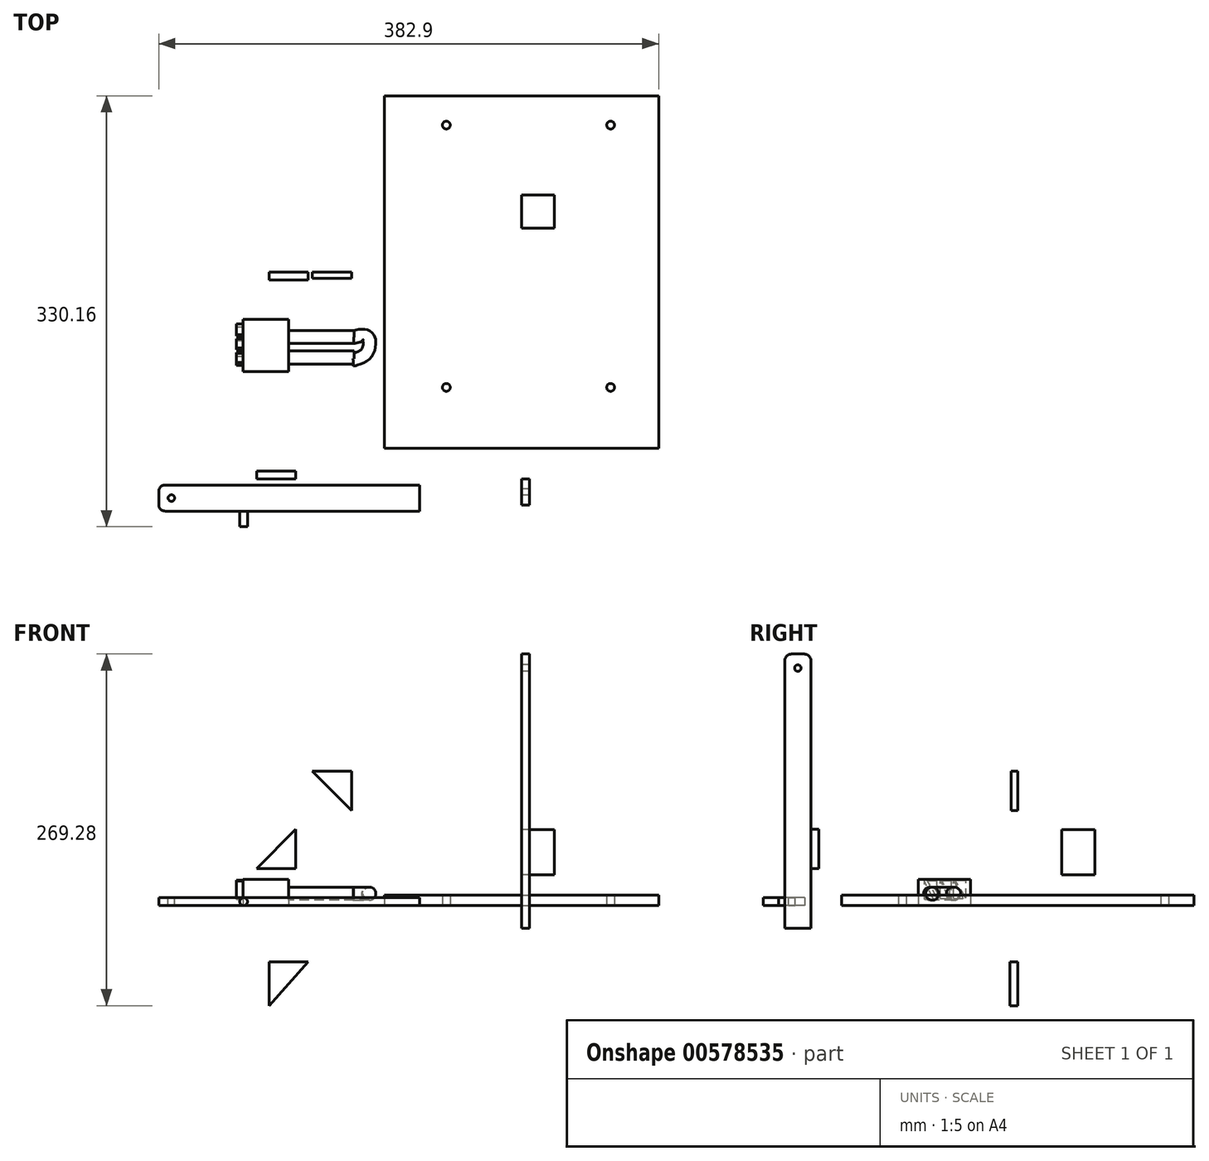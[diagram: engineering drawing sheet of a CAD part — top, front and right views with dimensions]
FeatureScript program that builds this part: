
annotation { "Feature Type Name" : "Feature", "Feature Type Description" : "" }
export const myFeature = defineFeature(function(context is Context, id is Id, definition is map)
    precondition{}
    {
        {
            var Q0;
            Q0=qCreatedBy(makeId("Top.planeOp"),FACE);
            var sketch = newSketch(context, id + "F0", { "sketchPlane" : qUnion([Q0])});
            skLineSegment(sketch, "E0.bottom", {"start": v(135, -105) * mm, "end": v(-135, -105) * mm});
            skLineSegment(sketch, "E0.top", {"start": v(135, 105) * mm, "end": v(-135, 105) * mm});
            skLineSegment(sketch, "E0.left", {"start": v(135, -105) * mm, "end": v(135, 105) * mm});
            skLineSegment(sketch, "E0.right", {"start": v(-135, -105) * mm, "end": v(-135, 105) * mm});
            skPoint(sketch, "E0.middle", {"position": v(0, 0) * mm});
            skCircle(sketch, "E1", {"center": v(-117.17, 88.39) * mm, "radius": 3 * mm});
            skCircle(sketch, "E2", {"center": v(-96.1, 99.53) * mm, "radius": 3 * mm});
            skCircle(sketch, "E3", {"center": v(-57.59, 112.52) * mm, "radius": 3 * mm});
            skCircle(sketch, "E4", {"center": v(68.25, 112.52) * mm, "radius": 3 * mm});
            skPoint(sketch, "E5", {"position": v(0, 112.52) * mm});
            skPoint(sketch, "E6", {"position": v(-57.59, -88.4) * mm});
            skCircle(sketch, "E7", {"center": v(-57.59, -88.4) * mm, "radius": 3 * mm});
            skPoint(sketch, "E8", {"position": v(68.25, -88.4) * mm});
            skCircle(sketch, "E9", {"center": v(68.25, -88.4) * mm, "radius": 3 * mm});
            skSolve(sketch);
        }
        {
            var Q0;
            Q0=makeQuery(id+"F0.imprint","IMPRINT",FACE,{"disambiguationData":[TD([[makeQuery(id+"F0.imprint","IMPRINT",EDGE,{"derivedFrom":sQuery(id+"F0.wireOp",EDGE,"E0.bottom")}),-1.0]])]});
            var sketch = newSketch(context, id + "F1", { "sketchPlane" : qUnion([Q0])});
            skCircle(sketch, "E10", {"center": v(176.37, 242.82) * mm, "radius": 60 * mm});
            skSolve(sketch);
        }
        {
            var Q0;
            Q0=makeQuery(id+"F0.imprint","IMPRINT",FACE,{"disambiguationData":[TD([[makeQuery(id+"F0.imprint","IMPRINT",EDGE,{"derivedFrom":sQuery(id+"F0.wireOp",EDGE,"E0.bottom")}),-1.0]])]});
            var sketch = newSketch(context, id + "F2", { "sketchPlane" : qUnion([Q0])});
            skLineSegment(sketch, "E11.bottom", {"start": v(-77.9, -163.16) * mm, "end": v(-277.9, -163.16) * mm});
            skLineSegment(sketch, "E11.top", {"start": v(-77.9, -183.16) * mm, "end": v(-277.9, -183.16) * mm});
            skLineSegment(sketch, "E11.left", {"start": v(-77.9, -163.16) * mm, "end": v(-77.9, -183.16) * mm});
            skLineSegment(sketch, "E11.right", {"start": v(-277.9, -163.16) * mm, "end": v(-277.9, -183.16) * mm});
            skPoint(sketch, "E11.middle", {"position": v(-177.9, -173.16) * mm});
            skSolve(sketch);
        }
        {
            var Q0;
            Q0=qCreatedBy(makeId("Right.planeOp"),FACE);
            var sketch = newSketch(context, id + "F3", { "sketchPlane" : qUnion([Q0])});
            skLineSegment(sketch, "E12.bottom", {"start": v(-158.53, -17.4) * mm, "end": v(-178.53, -17.4) * mm});
            skLineSegment(sketch, "E12.top", {"start": v(-158.53, 192.6) * mm, "end": v(-178.53, 192.6) * mm});
            skLineSegment(sketch, "E12.left", {"start": v(-158.53, -17.4) * mm, "end": v(-158.53, 192.6) * mm});
            skLineSegment(sketch, "E12.right", {"start": v(-178.53, -17.4) * mm, "end": v(-178.53, 192.6) * mm});
            skPoint(sketch, "E12.middle", {"position": v(-168.53, 87.6) * mm});
            skSolve(sketch);
        }
        {
            var Q0;
            Q0=makeQuery(id+"F2.imprint","IMPRINT",FACE,{"disambiguationData":[TD([[makeQuery(id+"F2.imprint","IMPRINT",EDGE,{"derivedFrom":sQuery(id+"F2.wireOp",EDGE,"E11.bottom")}),1.0]])]});
            extrude(context, id + "F4", {"entities" : qUnion([Q0]), "depth" : 6 * mm, "offsetDistance" : 25 * mm});
        }
        {
            var Q0;
            Q0=makeQuery(id+"F3.imprint","IMPRINT",FACE,{"disambiguationData":[TD([[makeQuery(id+"F3.imprint","IMPRINT",EDGE,{"derivedFrom":sQuery(id+"F3.wireOp",EDGE,"E12.bottom")}),-1.0]])]});
            extrude(context, id + "F5", {"entities" : qUnion([Q0]), "depth" : 6 * mm, "offsetDistance" : 25 * mm});
        }
        {
            var Q0;
            Q0=makeQuery(id+"F4.opExtrude","CAP_FACE",FACE,{"disambiguationData":[OSD([sQuery(id+"F2.wireOp",EDGE,"E11.bottom"),sQuery(id+"F2.wireOp",EDGE,"E11.top"),sQuery(id+"F2.wireOp",EDGE,"E11.left"),sQuery(id+"F2.wireOp",EDGE,"E11.right")])],"isStart":false});
            var sketch = newSketch(context, id + "F6", { "sketchPlane" : qUnion([Q0])});
            skLineSegment(sketch, "E13.0.0", {"start": v(-277.9, -183.16) * mm, "end": v(-77.9, -183.16) * mm});
            skLineSegment(sketch, "E13.0.1", {"start": v(-77.9, -183.16) * mm, "end": v(-77.9, -163.16) * mm});
            skLineSegment(sketch, "E13.0.2", {"start": v(-77.9, -163.16) * mm, "end": v(-277.9, -163.16) * mm});
            skLineSegment(sketch, "E13.0.3", {"start": v(-277.9, -163.16) * mm, "end": v(-277.9, -183.16) * mm});
            skPoint(sketch, "E14", {"position": v(-268.17, -173.16) * mm});
            skPoint(sketch, "E14.positionSnap0", {"position": v(-277.9, -173.16) * mm});
            skSolve(sketch);
        }
        {
            var Q0;
            Q0=sQuery(id+"F6.wireOp",VERTEX,"E14");
            var Q1;
            Q1=makeQuery(id+"F4.opExtrude","SWEPT_BODY",BODY,{"disambiguationData":[OSD([sQuery(id+"F2.wireOp",EDGE,"E11.bottom"),sQuery(id+"F2.wireOp",EDGE,"E11.top"),sQuery(id+"F2.wireOp",EDGE,"E11.left"),sQuery(id+"F2.wireOp",EDGE,"E11.right")])]});
            hole(context, id + "F7", {"style" : HoleStyle.SIMPLE, "endStyle" : HoleEndStyle.THROUGH, "holeDiameter" : 5 * mm, "isTappedThrough" : true, "tappedDepth" : 12 * mm, "tapClearance" : 3, "locations" : qUnion([Q0]), "scope" : qUnion([Q1])});
        }
        {
            var Q0;
            Q0=makeQuery(id+"F5.opExtrude","CAP_FACE",FACE,{"disambiguationData":[OSD([sQuery(id+"F3.wireOp",EDGE,"E12.bottom"),sQuery(id+"F3.wireOp",EDGE,"E12.top"),sQuery(id+"F3.wireOp",EDGE,"E12.left"),sQuery(id+"F3.wireOp",EDGE,"E12.right")])],"isStart":true});
            var sketch = newSketch(context, id + "F8", { "sketchPlane" : qUnion([Q0])});
            skLineSegment(sketch, "E15.0.0", {"start": v(158.53, 192.6) * mm, "end": v(158.53, -17.4) * mm});
            skLineSegment(sketch, "E15.0.1", {"start": v(158.53, -17.4) * mm, "end": v(178.53, -17.4) * mm});
            skLineSegment(sketch, "E15.0.2", {"start": v(178.53, -17.4) * mm, "end": v(178.53, 192.6) * mm});
            skLineSegment(sketch, "E15.0.3", {"start": v(178.53, 192.6) * mm, "end": v(158.53, 192.6) * mm});
            skPoint(sketch, "E16", {"position": v(168.53, 181.87) * mm});
            skPoint(sketch, "E16.positionSnap0", {"position": v(168.53, 192.6) * mm});
            skSolve(sketch);
        }
        {
            var Q0;
            Q0=sQuery(id+"F8.wireOp",VERTEX,"E16");
            var Q1;
            Q1=makeQuery(id+"F5.opExtrude","SWEPT_BODY",BODY,{"disambiguationData":[OSD([sQuery(id+"F3.wireOp",EDGE,"E12.bottom"),sQuery(id+"F3.wireOp",EDGE,"E12.top"),sQuery(id+"F3.wireOp",EDGE,"E12.left"),sQuery(id+"F3.wireOp",EDGE,"E12.right")])]});
            hole(context, id + "F9", {"style" : HoleStyle.SIMPLE, "endStyle" : HoleEndStyle.THROUGH, "holeDiameter" : 5 * mm, "isTappedThrough" : true, "tappedDepth" : 12 * mm, "tapClearance" : 3, "locations" : qUnion([Q0]), "scope" : qUnion([Q1])});
        }
        {
            var Q0;
            Q0=makeQuery(id+"F5.opExtrude","SWEPT_EDGE",EDGE,{"disambiguationData":[OSD([sQuery(id+"F3.wireOp",EDGE,"E12.top"),sQuery(id+"F3.wireOp",EDGE,"E12.right")])]});
            fillet(context, id + "F10", {"entities" : qUnion([Q0]), "radius" : 5 * mm, "tangentPropagation" : true, "allowEdgeOverflow" : false});
        }
        {
            var Q0;
            Q0=makeQuery(id+"F5.opExtrude","SWEPT_EDGE",EDGE,{"disambiguationData":[OSD([sQuery(id+"F3.wireOp",EDGE,"E12.top"),sQuery(id+"F3.wireOp",EDGE,"E12.left")])]});
            fillet(context, id + "F11", {"entities" : qUnion([Q0]), "radius" : 5 * mm, "tangentPropagation" : true, "allowEdgeOverflow" : false});
        }
        {
            var Q0;
            Q0=makeQuery(id+"F4.opExtrude","SWEPT_EDGE",EDGE,{"disambiguationData":[OSD([sQuery(id+"F2.wireOp",EDGE,"E11.top"),sQuery(id+"F2.wireOp",EDGE,"E11.right")])]});
            fillet(context, id + "F12", {"entities" : qUnion([Q0]), "radius" : 5 * mm, "tangentPropagation" : true, "allowEdgeOverflow" : false});
        }
        {
            var Q0;
            Q0=makeQuery(id+"F4.opExtrude","SWEPT_EDGE",EDGE,{"disambiguationData":[OSD([sQuery(id+"F2.wireOp",EDGE,"E11.bottom"),sQuery(id+"F2.wireOp",EDGE,"E11.right")])]});
            fillet(context, id + "F13", {"entities" : qUnion([Q0]), "radius" : 5 * mm, "tangentPropagation" : true, "allowEdgeOverflow" : false});
        }
        {
            var Q0;
            Q0=makeQuery(id+"F0.imprint","IMPRINT",FACE,{"disambiguationData":[TD([[makeQuery(id+"F0.imprint","IMPRINT",EDGE,{"derivedFrom":sQuery(id+"F0.wireOp",EDGE,"E0.bottom")}),-1.0]])]});
            var sketch = newSketch(context, id + "F14", { "sketchPlane" : qUnion([Q0])});
            skLineSegment(sketch, "E17.bottom", {"start": v(-105, -135) * mm, "end": v(105, -135) * mm});
            skLineSegment(sketch, "E17.top", {"start": v(-105, 135) * mm, "end": v(105, 135) * mm});
            skLineSegment(sketch, "E17.left", {"start": v(-105, -135) * mm, "end": v(-105, 135) * mm});
            skLineSegment(sketch, "E17.right", {"start": v(105, -135) * mm, "end": v(105, 135) * mm});
            skPoint(sketch, "E17.middle", {"position": v(0, 0) * mm});
            skSolve(sketch);
        }
        {
            var Q0;
            Q0 = qSketchRegion(id + "F14", true);
            extrude(context, id + "F15", {"entities" : qUnion([Q0]), "depth" : 8 * mm, "offsetDistance" : 25 * mm});
        }
        {
            var Q0;
            Q0=makeQuery(id+"F4.opExtrude","SWEPT_FACE",FACE,{"disambiguationData":[OSD([sQuery(id+"F2.wireOp",EDGE,"E11.top")])]});
            var sketch = newSketch(context, id + "F16", { "sketchPlane" : qUnion([Q0])});
            skLineSegment(sketch, "E18", {"start": v(-272.9, 0) * mm, "end": v(-212.9, 0) * mm});
            skLineSegment(sketch, "E19", {"start": v(-212.9, 0) * mm, "end": v(-212.9, 6) * mm});
            skCircle(sketch, "E20", {"center": v(-212.9, 3) * mm, "radius": 3 * mm});
            skSolve(sketch);
        }
        {
            var Q0;
            {var subQ0=sQuery(id+"F16.wireOp",EDGE,"E19");Q0=makeQuery(id+"F16.imprint","IMPRINT",FACE,{"disambiguationData":[TD([[makeQuery(id+"F16.imprint","IMPRINT",EDGE,{"derivedFrom":subQ0}),-1.0]])]});}
            var Q1;
            {var subQ0=sQuery(id+"F16.wireOp",EDGE,"E19");Q1=makeQuery(id+"F16.imprint","IMPRINT",FACE,{"disambiguationData":[TD([[makeQuery(id+"F16.imprint","IMPRINT",EDGE,{"derivedFrom":subQ0}),1.0]])]});}
            extrude(context, id + "F17", {"entities" : qUnion([Q0, Q1]), "operationType" : NewBodyOperationType.ADD, "depth" : 12 * mm, "offsetDistance" : 25 * mm});
        }
        {
            var Q0;
            Q0=makeQuery(id+"F1.imprint","IMPRINT",FACE,{"disambiguationData":[TD([[makeQuery(id+"F1.imprint","IMPRINT",EDGE,{"derivedFrom":sQuery(id+"F1.wireOp",EDGE,"E10")}),1.0]])]});
            extrude(context, id + "F18", {"entities" : qUnion([Q0]), "depth" : 6 * mm, "offsetDistance" : 25 * mm});
        }
        {
            var Q0;
            Q0=qCreatedBy(makeId("Right.planeOp"),FACE);
            var sketch = newSketch(context, id + "F19", { "sketchPlane" : qUnion([Q0])});
            skLineSegment(sketch, "E21.bottom", {"start": v(59.06, 58.09) * mm, "end": v(33.68, 58.09) * mm});
            skLineSegment(sketch, "E21.top", {"start": v(59.06, 23.62) * mm, "end": v(33.68, 23.62) * mm});
            skLineSegment(sketch, "E21.left", {"start": v(59.06, 58.09) * mm, "end": v(59.06, 23.62) * mm});
            skLineSegment(sketch, "E21.right", {"start": v(33.68, 58.09) * mm, "end": v(33.68, 23.62) * mm});
            skSolve(sketch);
        }
        {
            var Q0;
            Q0 = qSketchRegion(id + "F19", true);
            extrude(context, id + "F20", {"entities" : qUnion([Q0]), "depth" : 25 * mm, "offsetDistance" : 25 * mm});
        }
        {
            var Q0;
            Q0=makeQuery(id+"F5.opExtrude","SWEPT_FACE",FACE,{"disambiguationData":[OSD([sQuery(id+"F3.wireOp",EDGE,"E12.left")])]});
            var sketch = newSketch(context, id + "F21", { "sketchPlane" : qUnion([Q0])});
            skLineSegment(sketch, "E22", {"start": v(202.9, 28.37) * mm, "end": v(172.9, 28.37) * mm});
            skLineSegment(sketch, "E23", {"start": v(172.9, 28.37) * mm, "end": v(172.9, 58.37) * mm});
            skLineSegment(sketch, "E24", {"start": v(172.9, 58.37) * mm, "end": v(202.9, 28.37) * mm});
            skSolve(sketch);
        }
        {
            var Q0;
            Q0=makeQuery(id+"F21.imprint","IMPRINT",FACE,{"disambiguationData":[TD([[makeQuery(id+"F21.imprint","IMPRINT",EDGE,{"derivedFrom":sQuery(id+"F21.wireOp",EDGE,"E22")}),-1.0]])]});
            extrude(context, id + "F22", {"entities" : qUnion([Q0]), "depth" : 6 * mm, "offsetDistance" : 25 * mm});
        }
        {
            var Q0;
            Q0=qCreatedBy(makeId("Front.planeOp"),FACE);
            var sketch = newSketch(context, id + "F23", { "sketchPlane" : qUnion([Q0])});
            skLineSegment(sketch, "E25", {"start": v(-193.39, -76.68) * mm, "end": v(-193.39, -43.27) * mm});
            skLineSegment(sketch, "E26", {"start": v(-193.39, -43.27) * mm, "end": v(-163.39, -43.27) * mm});
            skLineSegment(sketch, "E27", {"start": v(-193.39, -76.68) * mm, "end": v(-163.39, -43.27) * mm});
            skSolve(sketch);
        }
        {
            var Q0;
            Q0=makeQuery(id+"F23.imprint","IMPRINT",FACE,{"disambiguationData":[TD([[makeQuery(id+"F23.imprint","IMPRINT",EDGE,{"derivedFrom":sQuery(id+"F23.wireOp",EDGE,"E25")}),-1.0]])]});
            extrude(context, id + "F24", {"entities" : qUnion([Q0]), "depth" : 6 * mm, "offsetDistance" : 25 * mm});
        }
        {
            var Q0;
            Q0=qCreatedBy(makeId("Front.planeOp"),FACE);
            var sketch = newSketch(context, id + "F25", { "sketchPlane" : qUnion([Q0])});
            skLineSegment(sketch, "E28", {"start": v(-130.15, 102.88) * mm, "end": v(-130.15, 72.88) * mm});
            skLineSegment(sketch, "E29", {"start": v(-130.15, 102.88) * mm, "end": v(-160.15, 102.88) * mm});
            skLineSegment(sketch, "E30", {"start": v(-130.15, 72.88) * mm, "end": v(-160.15, 102.88) * mm});
            skSolve(sketch);
        }
        {
            var Q0;
            Q0=makeQuery(id+"F25.imprint","IMPRINT",FACE,{"disambiguationData":[TD([[makeQuery(id+"F25.imprint","IMPRINT",EDGE,{"derivedFrom":sQuery(id+"F25.wireOp",EDGE,"E28")}),-1.0]])]});
            extrude(context, id + "F26", {"entities" : qUnion([Q0]), "depth" : 5 * mm, "offsetDistance" : 25 * mm});
        }
        {
            var Q0;
            Q0=makeQuery(id+"F0.imprint","IMPRINT",FACE,{"disambiguationData":[TD([[makeQuery(id+"F0.imprint","IMPRINT",EDGE,{"derivedFrom":sQuery(id+"F0.wireOp",EDGE,"E0.bottom")}),-1.0]])]});
            var sketch = newSketch(context, id + "F27", { "sketchPlane" : qUnion([Q0])});
            skLineSegment(sketch, "E31.bottom", {"start": v(-213.26, 76.23) * mm, "end": v(-178.26, 76.23) * mm});
            skLineSegment(sketch, "E31.top", {"start": v(-213.26, 36.23) * mm, "end": v(-178.26, 36.23) * mm});
            skLineSegment(sketch, "E31.left", {"start": v(-213.26, 76.23) * mm, "end": v(-213.26, 36.23) * mm});
            skLineSegment(sketch, "E31.right", {"start": v(-178.26, 76.23) * mm, "end": v(-178.26, 36.23) * mm});
            skSolve(sketch);
        }
        {
            var Q0;
            Q0=makeQuery(id+"F27.imprint","IMPRINT",FACE,{"disambiguationData":[TD([[makeQuery(id+"F27.imprint","IMPRINT",EDGE,{"derivedFrom":sQuery(id+"F27.wireOp",EDGE,"E31.bottom")}),-1.0]])]});
            extrude(context, id + "F28", {"entities" : qUnion([Q0]), "depth" : 20 * mm, "offsetDistance" : 25 * mm});
        }
        {
            var Q0;
            Q0=makeQuery(id+"F28.opExtrude","SWEPT_FACE",FACE,{"disambiguationData":[OSD([sQuery(id+"F27.wireOp",EDGE,"E31.left")])]});
            var sketch = newSketch(context, id + "F29", { "sketchPlane" : qUnion([Q0])});
            skLineSegment(sketch, "E32", {"start": v(-71.63, 4.77) * mm, "end": v(-71.63, 18.77) * mm});
            skLineSegment(sketch, "E33", {"start": v(-71.63, 4.77) * mm, "end": v(-64.63, 4.77) * mm});
            skLineSegment(sketch, "E34", {"start": v(-64.63, 4.77) * mm, "end": v(-71.63, 18.77) * mm});
            skSolve(sketch);
        }
        {
            var Q0;
            Q0=makeQuery(id+"F29.imprint","IMPRINT",FACE,{"disambiguationData":[TD([[makeQuery(id+"F29.imprint","IMPRINT",EDGE,{"derivedFrom":sQuery(id+"F29.wireOp",EDGE,"E32")}),-1.0]])]});
            extrude(context, id + "F30", {"entities" : qUnion([Q0]), "operationType" : NewBodyOperationType.ADD, "depth" : 5 * mm, "offsetDistance" : 25 * mm});
        }
        {
            var Q0;
            Q0=makeQuery(id+"F28.opExtrude","SWEPT_FACE",FACE,{"disambiguationData":[OSD([sQuery(id+"F27.wireOp",EDGE,"E31.left")])]});
            var sketch = newSketch(context, id + "F31", { "sketchPlane" : qUnion([Q0])});
            skLineSegment(sketch, "E35", {"start": v(-69.17, 19.23) * mm, "end": v(-62.17, 19.23) * mm});
            skLineSegment(sketch, "E36", {"start": v(-62.17, 19.23) * mm, "end": v(-61.7, 5.24) * mm});
            skLineSegment(sketch, "E37", {"start": v(-61.7, 5.24) * mm, "end": v(-69.17, 19.23) * mm});
            skSolve(sketch);
        }
        {
            var Q0;
            Q0=makeQuery(id+"F31.imprint","IMPRINT",FACE,{"disambiguationData":[TD([[makeQuery(id+"F31.imprint","IMPRINT",EDGE,{"derivedFrom":sQuery(id+"F31.wireOp",EDGE,"E35")}),1.0]])]});
            var sketch = newSketch(context, id + "F32", { "sketchPlane" : qUnion([Q0])});
            skLineSegment(sketch, "E38", {"start": v(-59.45, 5.28) * mm, "end": v(-59.45, 19.28) * mm});
            skLineSegment(sketch, "E39", {"start": v(-59.45, 5.28) * mm, "end": v(-52.45, 5.28) * mm});
            skLineSegment(sketch, "E40", {"start": v(-52.45, 5.28) * mm, "end": v(-59.45, 19.28) * mm});
            skSolve(sketch);
        }
        {
            var Q0;
            Q0=makeQuery(id+"F31.imprint","IMPRINT",FACE,{"disambiguationData":[TD([[makeQuery(id+"F31.imprint","IMPRINT",EDGE,{"derivedFrom":sQuery(id+"F31.wireOp",EDGE,"E35")}),1.0]])]});
            var sketch = newSketch(context, id + "F33", { "sketchPlane" : qUnion([Q0])});
            skLineSegment(sketch, "E41", {"start": v(-58.28, 19.15) * mm, "end": v(-51.28, 19.15) * mm});
            skLineSegment(sketch, "E42", {"start": v(-51.28, 19.15) * mm, "end": v(-51.28, 5.15) * mm});
            skLineSegment(sketch, "E43", {"start": v(-51.28, 5.15) * mm, "end": v(-58.28, 19.15) * mm});
            skSolve(sketch);
        }
        {
            var Q0;
            Q0=makeQuery(id+"F31.imprint","IMPRINT",FACE,{"disambiguationData":[TD([[makeQuery(id+"F31.imprint","IMPRINT",EDGE,{"derivedFrom":sQuery(id+"F31.wireOp",EDGE,"E35")}),1.0]])]});
            var sketch = newSketch(context, id + "F34", { "sketchPlane" : qUnion([Q0])});
            skLineSegment(sketch, "E44", {"start": v(-49.1, 5.46) * mm, "end": v(-42.1, 5.46) * mm});
            skLineSegment(sketch, "E45", {"start": v(-49.1, 5.46) * mm, "end": v(-49.1, 19.46) * mm});
            skLineSegment(sketch, "E46", {"start": v(-49.1, 19.46) * mm, "end": v(-42.1, 5.46) * mm});
            skSolve(sketch);
        }
        {
            var Q0;
            Q0=makeQuery(id+"F31.imprint","IMPRINT",FACE,{"disambiguationData":[TD([[makeQuery(id+"F31.imprint","IMPRINT",EDGE,{"derivedFrom":sQuery(id+"F31.wireOp",EDGE,"E35")}),1.0]])]});
            var sketch = newSketch(context, id + "F35", { "sketchPlane" : qUnion([Q0])});
            skLineSegment(sketch, "E47", {"start": v(-47.97, 19.3) * mm, "end": v(-39.8, 19.3) * mm});
            skLineSegment(sketch, "E48", {"start": v(-39.8, 5.66) * mm, "end": v(-47.97, 19.3) * mm});
            skLineSegment(sketch, "E49", {"start": v(-39.8, 5.66) * mm, "end": v(-39.8, 19.3) * mm});
            skSolve(sketch);
        }
        {
            var Q0;
            Q0=makeQuery(id+"F31.imprint","IMPRINT",FACE,{"disambiguationData":[TD([[makeQuery(id+"F31.imprint","IMPRINT",EDGE,{"derivedFrom":sQuery(id+"F31.wireOp",EDGE,"E35")}),-1.0]])]});
            extrude(context, id + "F36", {"entities" : qUnion([Q0]), "operationType" : NewBodyOperationType.ADD, "depth" : 5 * mm, "offsetDistance" : 25 * mm});
        }
        {
            var Q0;
            Q0=makeQuery(id+"F33.imprint","IMPRINT",FACE,{"disambiguationData":[TD([[makeQuery(id+"F33.imprint","IMPRINT",EDGE,{"derivedFrom":sQuery(id+"F33.wireOp",EDGE,"E41")}),-1.0]])]});
            extrude(context, id + "F37", {"entities" : qUnion([Q0]), "operationType" : NewBodyOperationType.ADD, "depth" : 5 * mm, "offsetDistance" : 25 * mm});
        }
        {
            var Q0;
            Q0=makeQuery(id+"F34.imprint","IMPRINT",FACE,{"disambiguationData":[TD([[makeQuery(id+"F34.imprint","IMPRINT",EDGE,{"derivedFrom":sQuery(id+"F34.wireOp",EDGE,"E44")}),1.0]])]});
            extrude(context, id + "F38", {"entities" : qUnion([Q0]), "operationType" : NewBodyOperationType.ADD, "depth" : 5 * mm, "offsetDistance" : 25 * mm});
        }
        {
            var Q0;
            Q0=makeQuery(id+"F35.imprint","IMPRINT",FACE,{"disambiguationData":[TD([[makeQuery(id+"F35.imprint","IMPRINT",EDGE,{"derivedFrom":sQuery(id+"F35.wireOp",EDGE,"E47")}),-1.0]])]});
            extrude(context, id + "F39", {"entities" : qUnion([Q0]), "operationType" : NewBodyOperationType.ADD, "depth" : 5 * mm, "offsetDistance" : 25 * mm});
        }
        {
            var Q0;
            Q0=makeQuery(id+"F32.imprint","IMPRINT",FACE,{"disambiguationData":[TD([[makeQuery(id+"F32.imprint","IMPRINT",EDGE,{"derivedFrom":sQuery(id+"F32.wireOp",EDGE,"E38")}),-1.0]])]});
            extrude(context, id + "F40", {"entities" : qUnion([Q0]), "operationType" : NewBodyOperationType.ADD, "depth" : 5 * mm, "offsetDistance" : 25 * mm});
        }
        {
            var Q0;
            Q0=makeQuery(id+"F28.opExtrude","SWEPT_FACE",FACE,{"disambiguationData":[OSD([sQuery(id+"F27.wireOp",EDGE,"E31.right")])]});
            var sketch = newSketch(context, id + "F41", { "sketchPlane" : qUnion([Q0])});
            skCircle(sketch, "E50", {"center": v(49.79, 9.07) * mm, "radius": 5 * mm});
            skCircle(sketch, "E51", {"center": v(65.54, 9.07) * mm, "radius": 5 * mm});
            skSolve(sketch);
        }
        {
            var Q0;
            Q0=makeQuery(id+"F41.imprint","IMPRINT",FACE,{"disambiguationData":[TD([[makeQuery(id+"F41.imprint","IMPRINT",EDGE,{"derivedFrom":sQuery(id+"F41.wireOp",EDGE,"E50")}),-1.0]])]});
            var sketch = newSketch(context, id + "F42", { "sketchPlane" : qUnion([Q0])});
            skSolve(sketch);
        }
        {
            var Q0;
            Q0=makeQuery(id+"F41.imprint","IMPRINT",FACE,{"disambiguationData":[TD([[makeQuery(id+"F41.imprint","IMPRINT",EDGE,{"derivedFrom":sQuery(id+"F41.wireOp",EDGE,"E51")}),1.0]])]});
            var sketch = newSketch(context, id + "F43", { "sketchPlane" : qUnion([Q0])});
            skSolve(sketch);
        }
        {
            var Q0;
            Q0 = qSketchRegion(id + "F43", true);
            var Q1;
            Q1=makeQuery(id+"F41.imprint","IMPRINT",FACE,{"disambiguationData":[TD([[makeQuery(id+"F41.imprint","IMPRINT",EDGE,{"derivedFrom":sQuery(id+"F41.wireOp",EDGE,"E51")}),1.0]])]});
            extrude(context, id + "F44", {"entities" : qUnion([Q0, Q1]), "operationType" : NewBodyOperationType.ADD, "depth" : 50 * mm, "offsetDistance" : 25 * mm});
        }
        {
            var Q0;
            Q0=makeQuery(id+"F42.imprint","IMPRINT",FACE,{"disambiguationData":[TD([[makeQuery(id+"F42.imprint","IMPRINT",EDGE,{"derivedFrom":makeQuery(id+"F41.imprint","IMPRINT",EDGE,{"derivedFrom":sQuery(id+"F41.wireOp",EDGE,"E50")})}),1.0]])]});
            extrude(context, id + "F45", {"entities" : qUnion([Q0]), "operationType" : NewBodyOperationType.ADD, "depth" : 50 * mm, "offsetDistance" : 25 * mm});
        }
        {
            var Q0;
            Q0=makeQuery(id+"F15.opExtrude","CAP_FACE",FACE,{"disambiguationData":[OSD([sQuery(id+"F14.wireOp",EDGE,"E17.bottom"),sQuery(id+"F14.wireOp",EDGE,"E17.top"),sQuery(id+"F14.wireOp",EDGE,"E17.left"),sQuery(id+"F14.wireOp",EDGE,"E17.right")])],"isStart":false});
            var sketch = newSketch(context, id + "F46", { "sketchPlane" : qUnion([Q0])});
            skFitSpline(sketch, "E52", {"points": [v(-128.51, 50.33) * mm, v(-118.22, 50.33) * mm, v(-118.74, 61.13) * mm, v(-129.03, 66.75) * mm], "startDerivative": vector(38.8, -9.62) * mm, "endDerivative": vector(-35.2, 9.6) * mm});
            skSolve(sketch);
        }
        {
            var Q0;
            Q0=makeQuery(id+"F45.opExtrude","CAP_FACE",FACE,{"disambiguationData":[OSD([sQuery(id+"F41.wireOp",EDGE,"E50")])],"isStart":false});
            var sketch = newSketch(context, id + "F47", { "sketchPlane" : qUnion([Q0])});
            skLineSegment(sketch, "E53", {"start": v(44.83, 8.43) * mm, "end": v(49.83, 8.43) * mm});
            skSolve(sketch);
        }
        {
            var Q0;
            Q0=makeQuery(id+"F47.imprint","IMPRINT",FACE,{"disambiguationData":[TD([[makeQuery(id+"F47.imprint","IMPRINT",EDGE,{"derivedFrom":makeQuery(id+"F45.opExtrude","CAP_EDGE",EDGE,{"disambiguationData":[OSD([sQuery(id+"F41.wireOp",EDGE,"E50")])],"isStart":false})}),1.0]])]});
            var Q1;
            Q1=sQuery(id+"F46.wireOp",EDGE,"E52");
            sweep(context, id + "F48", {"operationType" : NewBodyOperationType.ADD, "profiles" : qUnion([Q0]), "path" : qUnion([Q1])});
        }
        {
            var Q0;
            Q0=makeQuery(id+"F28.opExtrude","SWEPT_BODY",BODY,{"disambiguationData":[OSD([sQuery(id+"F27.wireOp",EDGE,"E31.bottom"),sQuery(id+"F27.wireOp",EDGE,"E31.top"),sQuery(id+"F27.wireOp",EDGE,"E31.left"),sQuery(id+"F27.wireOp",EDGE,"E31.right")])]});
            var Q1;
            Q1=qCreatedBy(makeId("Front.planeOp"),FACE);
            mirror(context, id + "F49", {"entities" : qUnion([Q0]), "mirrorPlane" : qUnion([Q1])});
        }
        {
            var Q0;
            Q0=sQuery(id+"F0.wireOp",VERTEX,"E3.center");
            var Q1;
            Q1=makeQuery(id+"F15.opExtrude","SWEPT_BODY",BODY,{"disambiguationData":[OSD([sQuery(id+"F14.wireOp",EDGE,"E17.bottom"),sQuery(id+"F14.wireOp",EDGE,"E17.top"),sQuery(id+"F14.wireOp",EDGE,"E17.left"),sQuery(id+"F14.wireOp",EDGE,"E17.right")])]});
            hole(context, id + "F50", {"style" : HoleStyle.SIMPLE, "endStyle" : HoleEndStyle.THROUGH, "oppositeDirection" : true, "holeDiameter" : 6 * mm, "majorDiameter" : 5 * mm, "isTappedThrough" : true, "tappedDepth" : 12 * mm, "tapClearance" : 3, "locations" : qUnion([Q0]), "scope" : qUnion([Q1])});
        }
        {
            var Q0;
            Q0=sQuery(id+"F0.wireOp",VERTEX,"E4.center");
            var Q1;
            Q1=makeQuery(id+"F15.opExtrude","SWEPT_BODY",BODY,{"disambiguationData":[OSD([sQuery(id+"F14.wireOp",EDGE,"E17.bottom"),sQuery(id+"F14.wireOp",EDGE,"E17.top"),sQuery(id+"F14.wireOp",EDGE,"E17.left"),sQuery(id+"F14.wireOp",EDGE,"E17.right")])]});
            hole(context, id + "F51", {"style" : HoleStyle.SIMPLE, "endStyle" : HoleEndStyle.THROUGH, "oppositeDirection" : true, "holeDiameter" : 6 * mm, "majorDiameter" : 5 * mm, "isTappedThrough" : true, "tappedDepth" : 12 * mm, "tapClearance" : 3, "locations" : qUnion([Q0]), "scope" : qUnion([Q1])});
        }
        {
            var Q0;
            Q0=sQuery(id+"F0.wireOp",VERTEX,"E6");
            var Q1;
            Q1=makeQuery(id+"F15.opExtrude","SWEPT_BODY",BODY,{"disambiguationData":[OSD([sQuery(id+"F14.wireOp",EDGE,"E17.bottom"),sQuery(id+"F14.wireOp",EDGE,"E17.top"),sQuery(id+"F14.wireOp",EDGE,"E17.left"),sQuery(id+"F14.wireOp",EDGE,"E17.right")])]});
            hole(context, id + "F52", {"style" : HoleStyle.SIMPLE, "endStyle" : HoleEndStyle.THROUGH, "oppositeDirection" : true, "holeDiameter" : 6 * mm, "majorDiameter" : 5 * mm, "isTappedThrough" : true, "tappedDepth" : 12 * mm, "tapClearance" : 3, "locations" : qUnion([Q0]), "scope" : qUnion([Q1])});
        }
        {
            var Q0;
            Q0=sQuery(id+"F0.wireOp",VERTEX,"E8");
            var Q1;
            Q1=makeQuery(id+"F15.opExtrude","SWEPT_BODY",BODY,{"disambiguationData":[OSD([sQuery(id+"F14.wireOp",EDGE,"E17.bottom"),sQuery(id+"F14.wireOp",EDGE,"E17.top"),sQuery(id+"F14.wireOp",EDGE,"E17.left"),sQuery(id+"F14.wireOp",EDGE,"E17.right")])]});
            hole(context, id + "F53", {"style" : HoleStyle.SIMPLE, "endStyle" : HoleEndStyle.THROUGH, "oppositeDirection" : true, "holeDiameter" : 6 * mm, "majorDiameter" : 5 * mm, "isTappedThrough" : true, "tappedDepth" : 12 * mm, "tapClearance" : 3, "locations" : qUnion([Q0]), "scope" : qUnion([Q1])});
        }
        {
            var Q0;
            Q0=makeQuery(id+"F18.opExtrude","SWEPT_BODY",BODY,{"disambiguationData":[OSD([sQuery(id+"F1.wireOp",EDGE,"E10")])]});
            deleteBodies(context, id + "F54", {"entities" : qUnion([Q0])});
        }
        {
            var Q0;
            Q0=makeQuery(id+"F4.opExtrude","SWEPT_FACE",FACE,{"disambiguationData":[OSD([sQuery(id+"F2.wireOp",EDGE,"E11.left")])]});
            var sketch = newSketch(context, id + "F55", { "sketchPlane" : qUnion([Q0])});
            skCircle(sketch, "E54", {"center": v(-174.22, 3.22) * mm, "radius": 1 * mm});
            skSolve(sketch);
        }
        {
            var Q0;
            Q0=sQuery(id+"F55.wireOp",EDGE,"E54");
            extrude(context, id + "F56", {"bodyType" : ToolBodyType.SURFACE, "surfaceEntities" : qUnion([Q0]), "depth" : 6 * mm, "offsetDistance" : 25 * mm});
        }
    });
